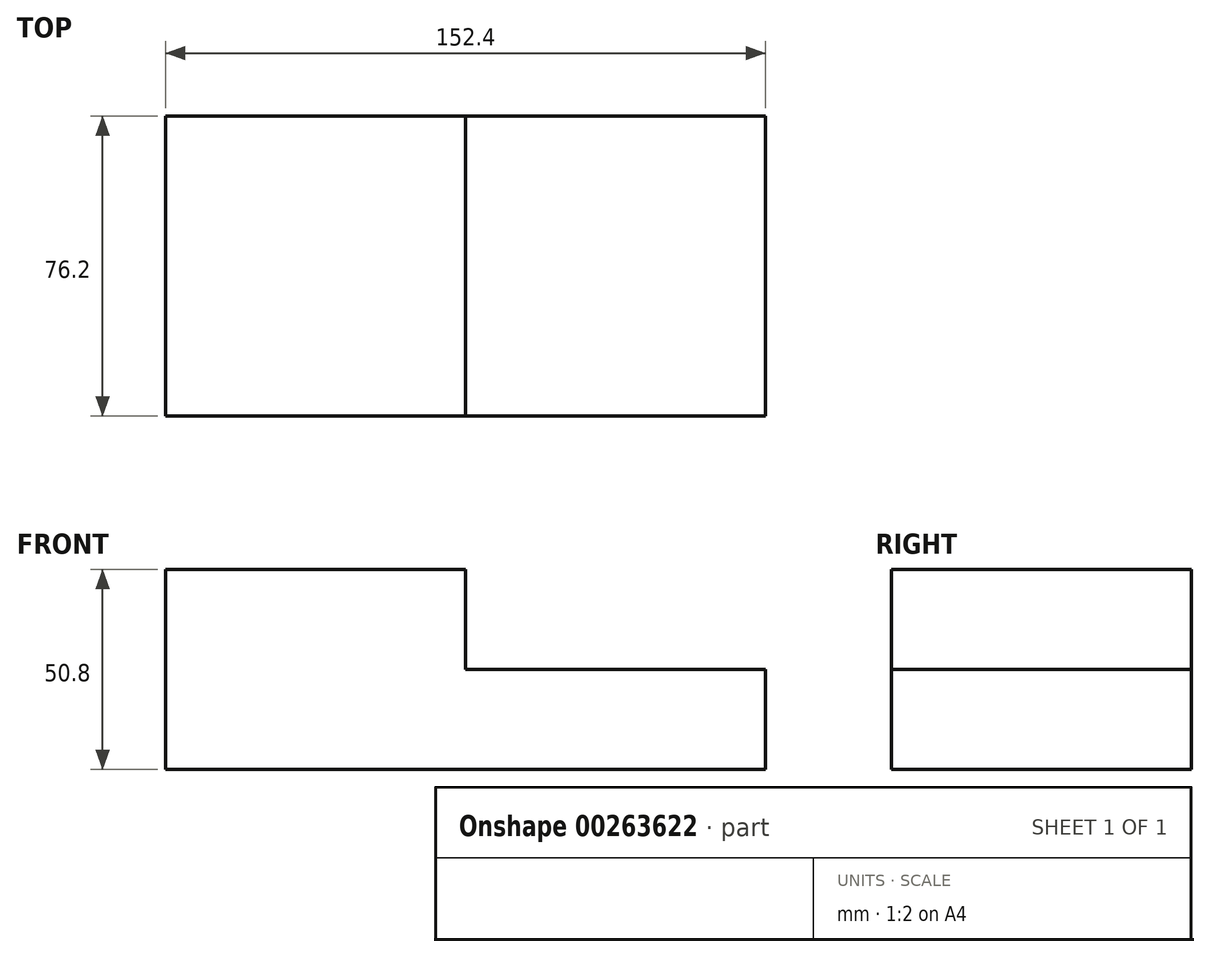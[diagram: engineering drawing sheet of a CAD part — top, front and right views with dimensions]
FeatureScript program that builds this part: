
annotation { "Feature Type Name" : "Feature", "Feature Type Description" : "" }
export const myFeature = defineFeature(function(context is Context, id is Id, definition is map)
    precondition{}
    {
        {
            var Q0;
            Q0=qCreatedBy(makeId("Front.planeOp"),FACE);
            var sketch = newSketch(context, id + "F0", { "sketchPlane" : qUnion([Q0])});
            skLineSegment(sketch, "E0.bottom", {"start": v(0, 0) * mm, "end": v(152.4, 0) * mm});
            skLineSegment(sketch, "E0.top", {"start": v(76.2, 25.4) * mm, "end": v(152.4, 25.4) * mm});
            skLineSegment(sketch, "E0.left", {"start": v(0, 0) * mm, "end": v(0, 25.4) * mm});
            skLineSegment(sketch, "E0.right", {"start": v(152.4, 0) * mm, "end": v(152.4, 25.4) * mm});
            skLineSegment(sketch, "E1.top", {"start": v(0, 50.8) * mm, "end": v(76.2, 50.8) * mm});
            skLineSegment(sketch, "E1.left", {"start": v(0, 25.4) * mm, "end": v(0, 50.8) * mm});
            skLineSegment(sketch, "E1.right", {"start": v(76.2, 25.4) * mm, "end": v(76.2, 50.8) * mm});
            skSolve(sketch);
        }
        {
            var Q0;
            Q0=makeQuery(id+"F0.imprint","IMPRINT",FACE,{"disambiguationData":[TD([[makeQuery(id+"F0.imprint","IMPRINT",EDGE,{"derivedFrom":sQuery(id+"F0.wireOp",EDGE,"E0.bottom")}),1.0]])]});
            extrude(context, id + "F1", {"entities" : qUnion([Q0]), "depth" : 76.2 * mm});
        }
    });
